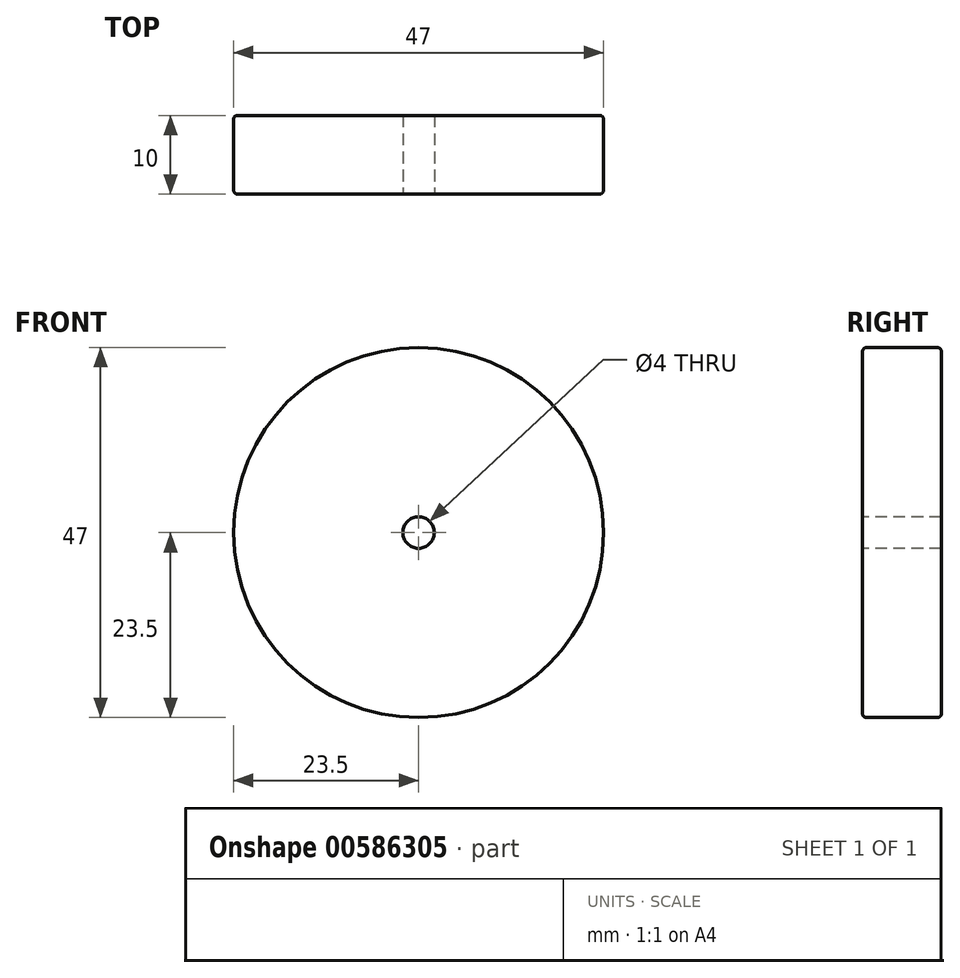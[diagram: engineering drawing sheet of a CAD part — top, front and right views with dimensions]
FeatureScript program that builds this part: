
annotation { "Feature Type Name" : "Feature", "Feature Type Description" : "" }
export const myFeature = defineFeature(function(context is Context, id is Id, definition is map)
    precondition{}
    {
        {
            var Q0;
            Q0=qCreatedBy(makeId("Front.planeOp"),FACE);
            var sketch = newSketch(context, id + "F0", { "sketchPlane" : qUnion([Q0])});
            skCircle(sketch, "E0", {"center": v(0, 0) * mm, "radius": 23.5 * mm});
            skSolve(sketch);
        }
        {
            var Q0;
            Q0=makeQuery(id+"F0.imprint","IMPRINT",FACE,{"disambiguationData":[TD([[makeQuery(id+"F0.imprint","IMPRINT",EDGE,{"derivedFrom":sQuery(id+"F0.wireOp",EDGE,"E0")}),1.0]])]});
            extrude(context, id + "F1", {"entities" : qUnion([Q0]), "depth" : 10 * mm, "offsetDistance" : 25.4 * mm});
        }
        {
            var Q0;
            Q0=makeQuery(id+"F1.opExtrude","CAP_FACE",FACE,{"disambiguationData":[OSD([sQuery(id+"F0.wireOp",EDGE,"E0")])],"isStart":false});
            var sketch = newSketch(context, id + "F2", { "sketchPlane" : qUnion([Q0])});
            skCircle(sketch, "E1", {"center": v(0, 0) * mm, "radius": 2 * mm});
            skSolve(sketch);
        }
        {
            var Q0;
            Q0=makeQuery(id+"F2.imprint","IMPRINT",FACE,{"disambiguationData":[TD([[makeQuery(id+"F2.imprint","IMPRINT",EDGE,{"derivedFrom":sQuery(id+"F2.wireOp",EDGE,"E1")}),1.0]])]});
            extrude(context, id + "F3", {"entities" : qUnion([Q0]), "operationType" : NewBodyOperationType.REMOVE, "oppositeDirection" : true, "depth" : 25.4 * mm, "offsetDistance" : 25.4 * mm});
        }
        {
            var Q0;
            Q0=makeQuery(id+"F1.opExtrude","CAP_EDGE",EDGE,{"disambiguationData":[OSD([sQuery(id+"F0.wireOp",EDGE,"E0")])],"isStart":false});
            var Q1;
            Q1=makeQuery(id+"F1.opExtrude","CAP_EDGE",EDGE,{"disambiguationData":[OSD([sQuery(id+"F0.wireOp",EDGE,"E0")])],"isStart":true});
            fillet(context, id + "F4", {"entities" : qUnion([Q0, Q1]), "radius" : 0.5 * mm, "tangentPropagation" : true, "allowEdgeOverflow" : false});
        }
    });
